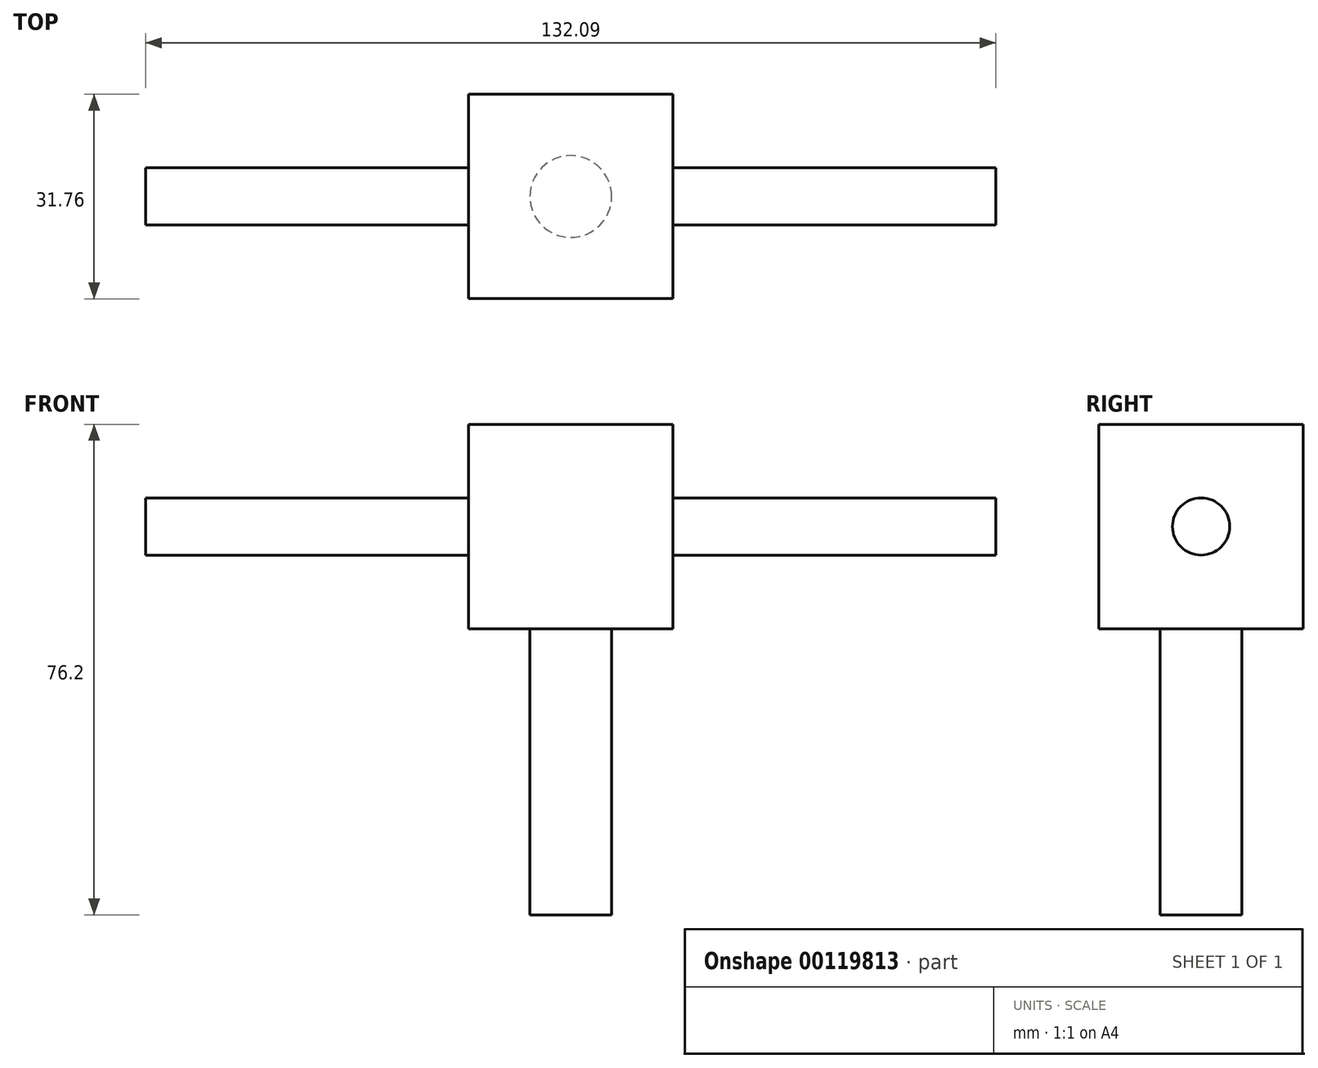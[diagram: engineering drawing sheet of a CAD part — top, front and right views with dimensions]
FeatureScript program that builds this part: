
annotation { "Feature Type Name" : "Feature", "Feature Type Description" : "" }
export const myFeature = defineFeature(function(context is Context, id is Id, definition is map)
    precondition{}
    {
        {
            var Q0;
            Q0=qCreatedBy(makeId("Front.planeOp"),FACE);
            var sketch = newSketch(context, id + "F0", { "sketchPlane" : qUnion([Q0])});
            skLineSegment(sketch, "E0.bottom", {"start": v(0, 0) * mm, "end": v(-31.75, 0) * mm});
            skLineSegment(sketch, "E0.top", {"start": v(0, 31.75) * mm, "end": v(-31.75, 31.75) * mm});
            skLineSegment(sketch, "E0.left", {"start": v(0, 0) * mm, "end": v(0, 31.75) * mm});
            skLineSegment(sketch, "E0.right", {"start": v(-31.75, 0) * mm, "end": v(-31.75, 31.75) * mm});
            skSolve(sketch);
        }
        {
            var Q0;
            Q0 = qSketchRegion(id + "F0", true);
            extrude(context, id + "F1", {"entities" : qUnion([Q0]), "endBound" : BoundingType.SYMMETRIC, "depth" : 31.75 * mm});
        }
        {
            var Q0;
            Q0=makeQuery(id+"F1.opExtrude","SWEPT_FACE",FACE,{"disambiguationData":[OSD([sQuery(id+"F0.wireOp",EDGE,"E0.left")])]});
            var sketch = newSketch(context, id + "F2", { "sketchPlane" : qUnion([Q0])});
            skCircle(sketch, "E1", {"center": v(0, 15.88) * mm, "radius": 4.45 * mm});
            skSolve(sketch);
        }
        {
            var Q0;
            Q0=makeQuery(id+"F2.imprint","IMPRINT",FACE,{"disambiguationData":[TD([[makeQuery(id+"F2.imprint","IMPRINT",EDGE,{"derivedFrom":sQuery(id+"F2.wireOp",EDGE,"E1")}),1.0]])]});
            extrude(context, id + "F3", {"entities" : qUnion([Q0]), "operationType" : NewBodyOperationType.ADD, "depth" : 50.16 * mm, "hasSecondDirection" : true, "secondDirectionOppositeDirection" : true, "secondDirectionDepth" : 81.9 * mm});
        }
        {
            var Q0;
            Q0=makeQuery(id+"F1.opExtrude","SWEPT_FACE",FACE,{"disambiguationData":[OSD([sQuery(id+"F0.wireOp",EDGE,"E0.bottom")])]});
            var sketch = newSketch(context, id + "F4", { "sketchPlane" : qUnion([Q0])});
            skCircle(sketch, "E2", {"center": v(-15.88, 0) * mm, "radius": 6.35 * mm});
            skPoint(sketch, "E2.centerSnap0", {"position": v(-15.88, -15.88) * mm});
            skSolve(sketch);
        }
        {
            var Q0;
            Q0 = qSketchRegion(id + "F4", true);
            extrude(context, id + "F5", {"entities" : qUnion([Q0]), "operationType" : NewBodyOperationType.ADD, "depth" : 44.45 * mm});
        }
    });
